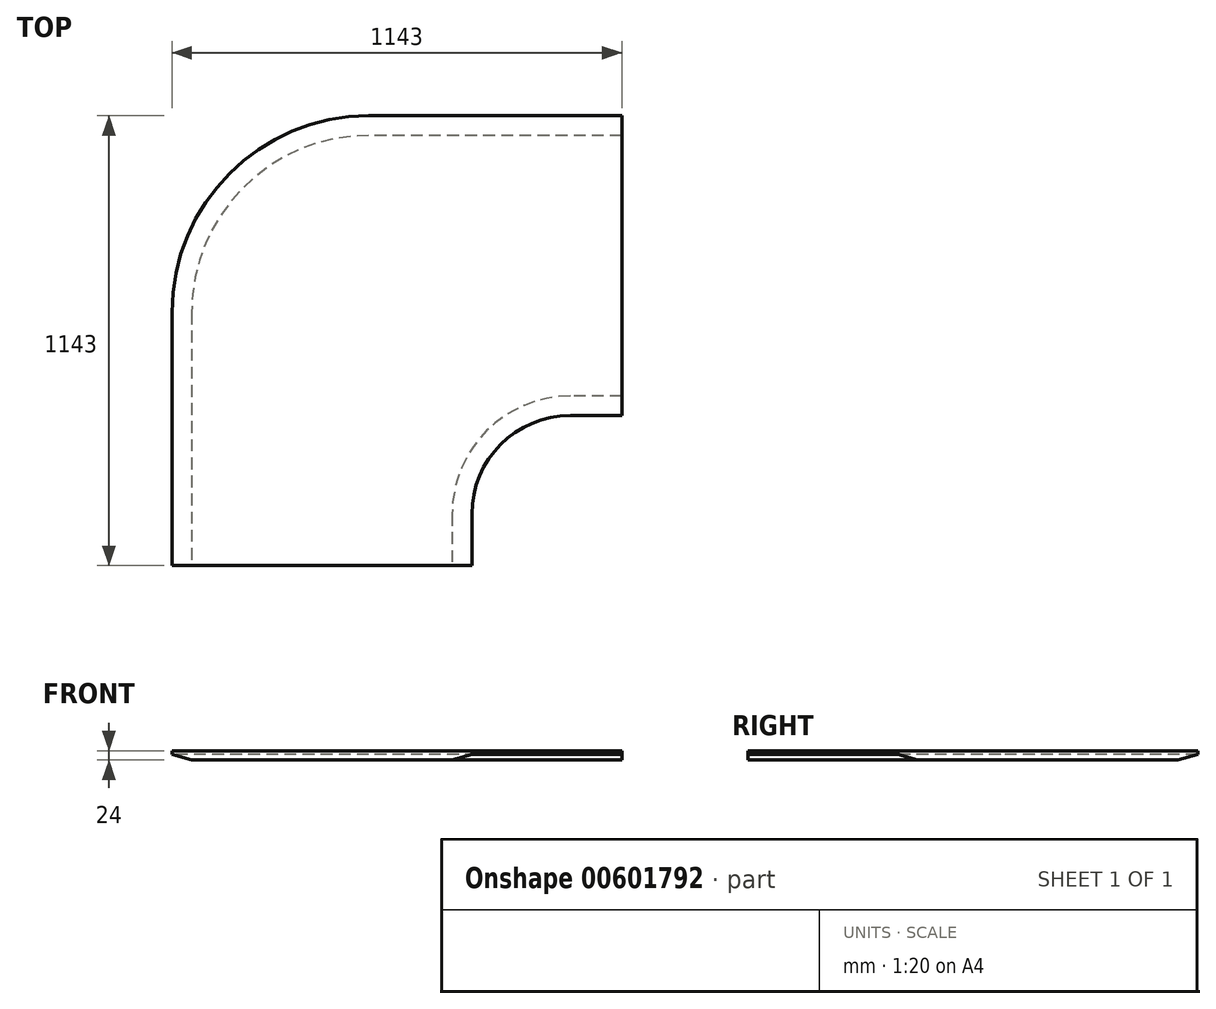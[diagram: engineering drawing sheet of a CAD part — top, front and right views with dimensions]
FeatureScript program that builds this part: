
annotation { "Feature Type Name" : "Feature", "Feature Type Description" : "" }
export const myFeature = defineFeature(function(context is Context, id is Id, definition is map)
    precondition{}
    {
        {
            var Q0;
            Q0=qCreatedBy(makeId("Top.planeOp"),FACE);
            var sketch = newSketch(context, id + "F0", { "sketchPlane" : qUnion([Q0])});
            skLineSegment(sketch, "E0", {"start": v(0, 0) * mm, "end": v(0, 762) * mm});
            skLineSegment(sketch, "E1", {"start": v(0, 762) * mm, "end": v(-643, 762) * mm});
            skLineSegment(sketch, "E2", {"start": v(-1143, 262) * mm, "end": v(-1143, -381) * mm});
            skLineSegment(sketch, "E3", {"start": v(-1143, -381) * mm, "end": v(-381, -381) * mm});
            skLineSegment(sketch, "E4", {"start": v(-1143, 762) * mm, "end": v(-381, 0) * mm, "construction": true});
            skLineSegment(sketch, "E5", {"start": v(-381, -381) * mm, "end": v(-381, -250) * mm});
            skLineSegment(sketch, "E6", {"start": v(-131, 0) * mm, "end": v(0, 0) * mm});
            skPoint(sketch, "E7.visualSharp", {"position": v(-1143, 762) * mm});
            skArc(sketch, "E7.filletArc", {"start": v(-643, 762) * mm, "mid": v(-996.55, 615.55) * mm, "end": v(-1143, 262) * mm});
            skPoint(sketch, "E8.visualSharp", {"position": v(-381, 0) * mm});
            skArc(sketch, "E8.filletArc", {"start": v(-131, 0) * mm, "mid": v(-307.78, -73.22) * mm, "end": v(-381, -250) * mm});
            skSolve(sketch);
        }
        {
            var Q0;
            Q0=qSketchRegion(id+"F0",true);
            extrude(context, id + "F1", {"entities" : qUnion([Q0]), "depth" : 24 * mm, "offsetDistance" : 25.4 * mm});
        }
        {
            var Q0;
            Q0=makeQuery(id+"F1.opExtrude","SWEPT_FACE",FACE,{"disambiguationData":[OSD([sQuery(id+"F0.wireOp",EDGE,"E0")])]});
            var sketch = newSketch(context, id + "F2", { "sketchPlane" : qUnion([Q0])});
            skLineSegment(sketch, "E9", {"start": v(762, 14) * mm, "end": v(712, 0) * mm});
            skLineSegment(sketch, "E10", {"start": v(712, 0) * mm, "end": v(762, 0) * mm});
            skLineSegment(sketch, "E11", {"start": v(762, 0) * mm, "end": v(762, 14) * mm});
            skLineSegment(sketch, "E12", {"start": v(0, 14) * mm, "end": v(50, 0) * mm});
            skLineSegment(sketch, "E13", {"start": v(50, 0) * mm, "end": v(0, 0) * mm});
            skLineSegment(sketch, "E14", {"start": v(0, 0) * mm, "end": v(0, 14) * mm});
            skSolve(sketch);
        }
        {
            var Q0;
            Q0=makeQuery(id+"F1.opExtrude","CAP_FACE",FACE,{"disambiguationData":[OSD([sQuery(id+"F0.wireOp",EDGE,"E0"),sQuery(id+"F0.wireOp",EDGE,"E1"),sQuery(id+"F0.wireOp",EDGE,"E2"),sQuery(id+"F0.wireOp",EDGE,"E3"),sQuery(id+"F0.wireOp",EDGE,"E5"),sQuery(id+"F0.wireOp",EDGE,"E6"),sQuery(id+"F0.wireOp",EDGE,"E7.filletArc"),sQuery(id+"F0.wireOp",EDGE,"E8.filletArc")])],"isStart":true});
            var sketch = newSketch(context, id + "F3", { "sketchPlane" : qUnion([Q0])});
            skLineSegment(sketch, "E15.0", {"start": v(-381, 381) * mm, "end": v(-381, 250) * mm});
            skArc(sketch, "E16.0", {"start": v(-131, 0) * mm, "mid": v(-307.78, 73.22) * mm, "end": v(-381, 250) * mm});
            skLineSegment(sketch, "E17.0", {"start": v(-131, 0) * mm, "end": v(0, 0) * mm});
            skLineSegment(sketch, "E18.0", {"start": v(-1143, -262) * mm, "end": v(-1143, 381) * mm});
            skArc(sketch, "E19.0", {"start": v(-643, -762) * mm, "mid": v(-996.55, -615.55) * mm, "end": v(-1143, -262) * mm});
            skLineSegment(sketch, "E20.0", {"start": v(0, -762) * mm, "end": v(-643, -762) * mm});
            skSolve(sketch);
        }
        {
            var Q0;
            Q0=makeQuery(id+"F2.imprint","IMPRINT",FACE,{"disambiguationData":[TD([[makeQuery(id+"F2.imprint","IMPRINT",EDGE,{"derivedFrom":sQuery(id+"F2.wireOp",EDGE,"E12")}),-1.0]])]});
            var Q1;
            Q1=sQuery(id+"F3.wireOp",EDGE,"E17.0");
            var Q2;
            Q2=sQuery(id+"F3.wireOp",EDGE,"E15.0");
            var Q3;
            Q3=sQuery(id+"F3.wireOp",EDGE,"E16.0");
            sweep(context, id + "F4", {"operationType" : NewBodyOperationType.REMOVE, "profiles" : qUnion([Q0]), "path" : qUnion([Q1, Q2, Q3])});
        }
        {
            var Q0;
            Q0=makeQuery(id+"F2.imprint","IMPRINT",FACE,{"disambiguationData":[TD([[makeQuery(id+"F2.imprint","IMPRINT",EDGE,{"derivedFrom":sQuery(id+"F2.wireOp",EDGE,"E9")}),1.0]])]});
            var Q1;
            Q1=sQuery(id+"F3.wireOp",EDGE,"E20.0");
            var Q2;
            Q2=sQuery(id+"F3.wireOp",EDGE,"E19.0");
            var Q3;
            Q3=sQuery(id+"F3.wireOp",EDGE,"E18.0");
            sweep(context, id + "F5", {"operationType" : NewBodyOperationType.REMOVE, "profiles" : qUnion([Q0]), "path" : qUnion([Q1, Q2, Q3])});
        }
    });
